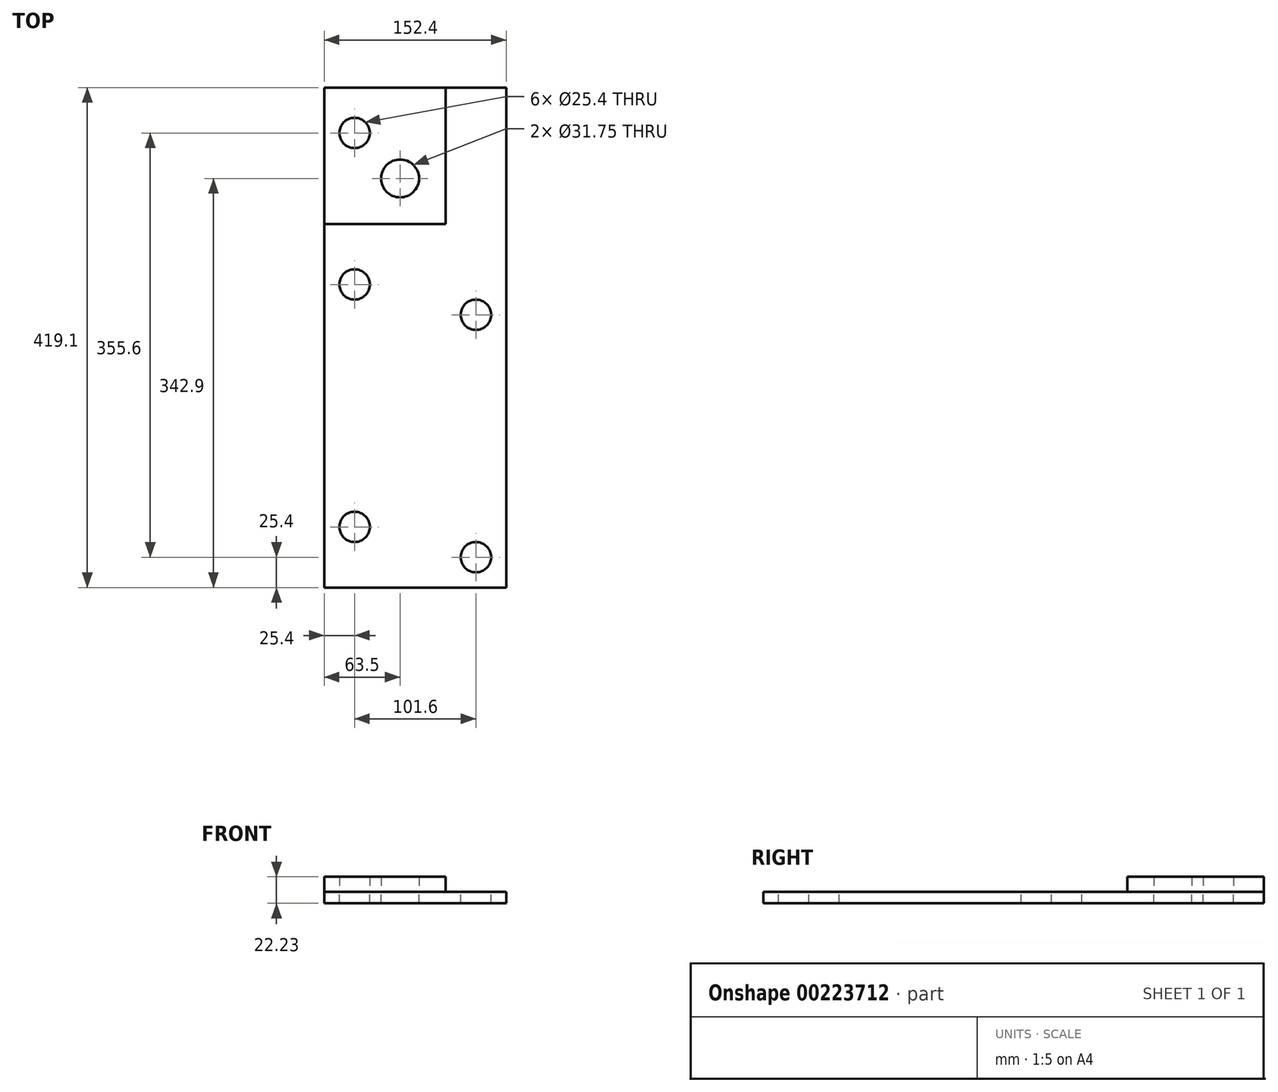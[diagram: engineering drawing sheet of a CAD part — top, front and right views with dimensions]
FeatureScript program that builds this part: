
annotation { "Feature Type Name" : "Feature", "Feature Type Description" : "" }
export const myFeature = defineFeature(function(context is Context, id is Id, definition is map)
    precondition{}
    {
        {
            var Q0;
            Q0=qCreatedBy(makeId("Top.planeOp"),FACE);
            var sketch = newSketch(context, id + "F0", { "sketchPlane" : qUnion([Q0])});
            skLineSegment(sketch, "E0.bottom", {"start": v(-63.5, 76.2) * mm, "end": v(38.1, 76.2) * mm});
            skLineSegment(sketch, "E0.top", {"start": v(-63.5, -38.1) * mm, "end": v(38.1, -38.1) * mm});
            skLineSegment(sketch, "E0.left", {"start": v(-63.5, 76.2) * mm, "end": v(-63.5, -38.1) * mm});
            skLineSegment(sketch, "E0.right", {"start": v(38.1, 76.2) * mm, "end": v(38.1, -38.1) * mm});
            skCircle(sketch, "E1", {"center": v(0, 0) * mm, "radius": 15.88 * mm});
            skCircle(sketch, "E2", {"center": v(-38.1, 38.1) * mm, "radius": 12.7 * mm});
            skSolve(sketch);
        }
        {
            var Q0;
            Q0=makeQuery(id+"F0.imprint","IMPRINT",FACE,{"disambiguationData":[TD([[makeQuery(id+"F0.imprint","IMPRINT",EDGE,{"derivedFrom":sQuery(id+"F0.wireOp",EDGE,"E0.bottom")}),-1.0]])]});
            extrude(context, id + "F1", {"entities" : qUnion([Q0]), "depth" : 12.7 * mm});
        }
        {
            var Q0;
            Q0=makeQuery(id+"F1.opExtrude","CAP_FACE",FACE,{"disambiguationData":[OSD([sQuery(id+"F0.wireOp",EDGE,"E0.bottom"),sQuery(id+"F0.wireOp",EDGE,"E0.top"),sQuery(id+"F0.wireOp",EDGE,"E0.left"),sQuery(id+"F0.wireOp",EDGE,"E0.right"),sQuery(id+"F0.wireOp",EDGE,"E1"),sQuery(id+"F0.wireOp",EDGE,"E2")])],"isStart":true});
            var sketch = newSketch(context, id + "F2", { "sketchPlane" : qUnion([Q0])});
            skCircle(sketch, "E3.0", {"center": v(-38.1, -38.1) * mm, "radius": 12.7 * mm});
            skCircle(sketch, "E4.0", {"center": v(0, 0) * mm, "radius": 15.88 * mm});
            skPoint(sketch, "E5.0", {"position": v(-63.5, -76.2) * mm});
            skPoint(sketch, "E6.0", {"position": v(-63.5, 38.1) * mm});
            skLineSegment(sketch, "E7.bottom", {"start": v(-63.5, -76.2) * mm, "end": v(88.9, -76.2) * mm});
            skLineSegment(sketch, "E7.top", {"start": v(-63.5, 342.9) * mm, "end": v(88.9, 342.9) * mm});
            skLineSegment(sketch, "E7.left", {"start": v(-63.5, -76.2) * mm, "end": v(-63.5, 342.9) * mm});
            skLineSegment(sketch, "E7.right", {"start": v(88.9, -76.2) * mm, "end": v(88.9, 342.9) * mm});
            skCircle(sketch, "E8", {"center": v(63.5, 317.5) * mm, "radius": 12.7 * mm});
            skCircle(sketch, "E9", {"center": v(-38.1, 292.1) * mm, "radius": 12.7 * mm});
            skCircle(sketch, "E10", {"center": v(63.5, 114.3) * mm, "radius": 12.7 * mm});
            skCircle(sketch, "E11", {"center": v(-38.1, 88.9) * mm, "radius": 12.7 * mm});
            skSolve(sketch);
        }
        {
            var Q0;
            {var subQ3=sQuery(id+"F2.wireOp",EDGE,"E7.top");Q0=makeQuery(id+"F2.imprint","IMPRINT",FACE,{"disambiguationData":[TD([[makeQuery(id+"F2.imprint","IMPRINT",EDGE,{"derivedFrom":subQ3}),-1.0]])]});}
            var Q1;
            Q1=makeQuery(id+"F2.imprint","IMPRINT",FACE,{"disambiguationData":[TD([[makeQuery(id+"F2.imprint","IMPRINT",EDGE,{"derivedFrom":sQuery(id+"F2.wireOp",EDGE,"E3.0")}),1.0]])]});
            extrude(context, id + "F3", {"entities" : qUnion([Q0, Q1]), "depth" : 9.52 * mm});
        }
    });
